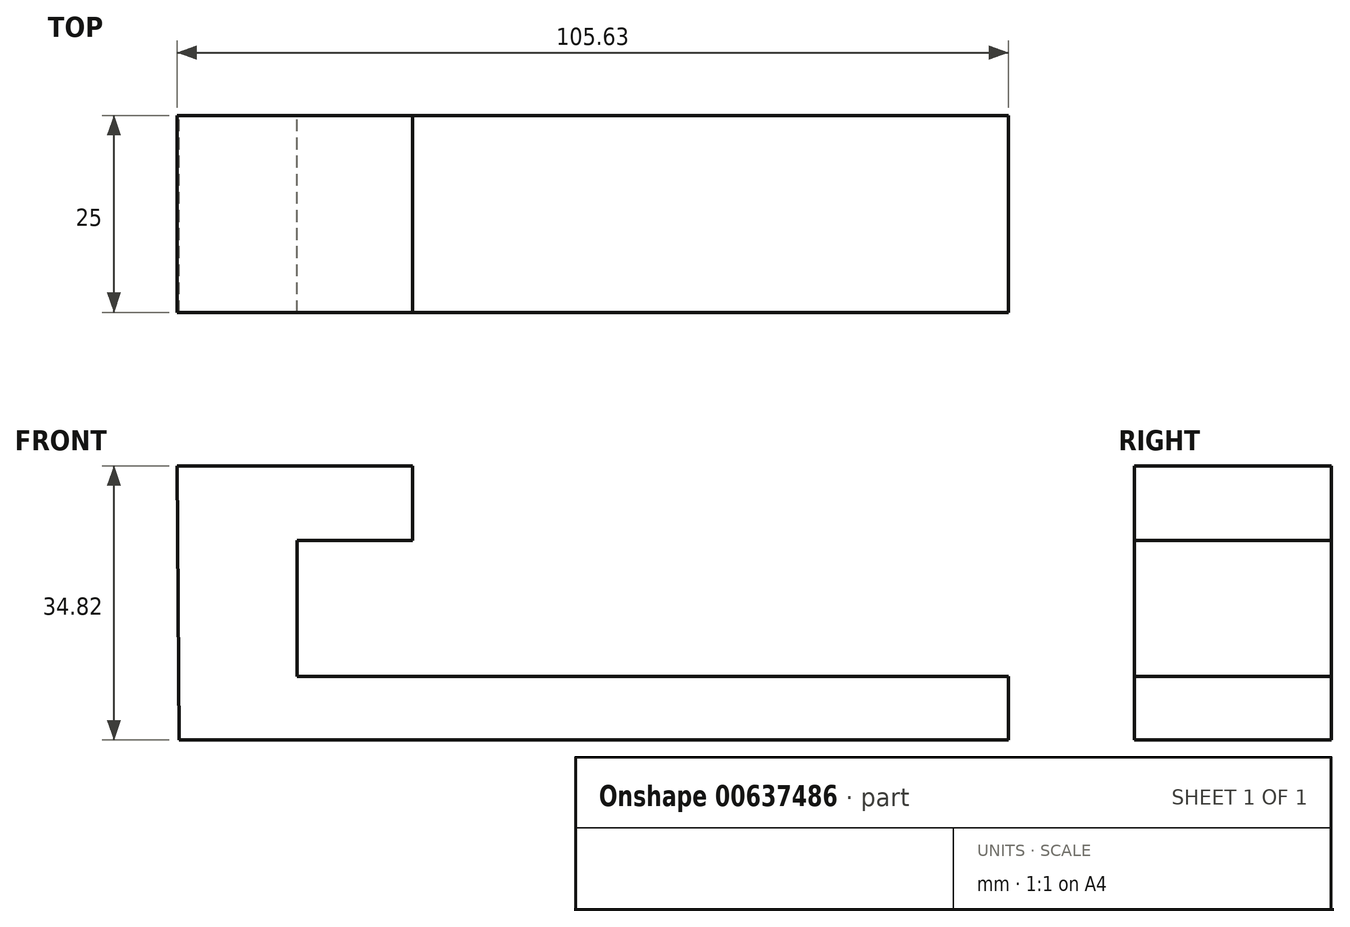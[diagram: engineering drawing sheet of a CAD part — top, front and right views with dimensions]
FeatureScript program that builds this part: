
annotation { "Feature Type Name" : "Feature", "Feature Type Description" : "" }
export const myFeature = defineFeature(function(context is Context, id is Id, definition is map)
    precondition{}
    {
        {
            var Q0;
            Q0=qCreatedBy(makeId("Front.planeOp"),FACE);
            var sketch = newSketch(context, id + "F0", { "sketchPlane" : qUnion([Q0])});
            skLineSegment(sketch, "E0", {"start": v(-51.66, -50.22) * mm, "end": v(53.68, -50.22) * mm});
            skLineSegment(sketch, "E1", {"start": v(53.68, -50.22) * mm, "end": v(53.68, -42.16) * mm});
            skLineSegment(sketch, "E2", {"start": v(53.68, -42.16) * mm, "end": v(-36.7, -42.16) * mm});
            skLineSegment(sketch, "E3", {"start": v(-36.7, -42.16) * mm, "end": v(-36.7, -24.9) * mm});
            skLineSegment(sketch, "E4", {"start": v(-36.7, -24.9) * mm, "end": v(-22.02, -24.9) * mm});
            skLineSegment(sketch, "E5", {"start": v(-22.02, -24.9) * mm, "end": v(-22.02, -15.4) * mm});
            skLineSegment(sketch, "E6", {"start": v(-22.02, -15.4) * mm, "end": v(-51.95, -15.4) * mm});
            skLineSegment(sketch, "E7", {"start": v(-51.95, -15.4) * mm, "end": v(-51.66, -50.22) * mm});
            skSolve(sketch);
        }
        {
            var Q0;
            Q0 = qSketchRegion(id + "F0", true);
            extrude(context, id + "F1", {"entities" : qUnion([Q0]), "depth" : 25 * mm, "offsetDistance" : 25 * mm});
        }
    });
